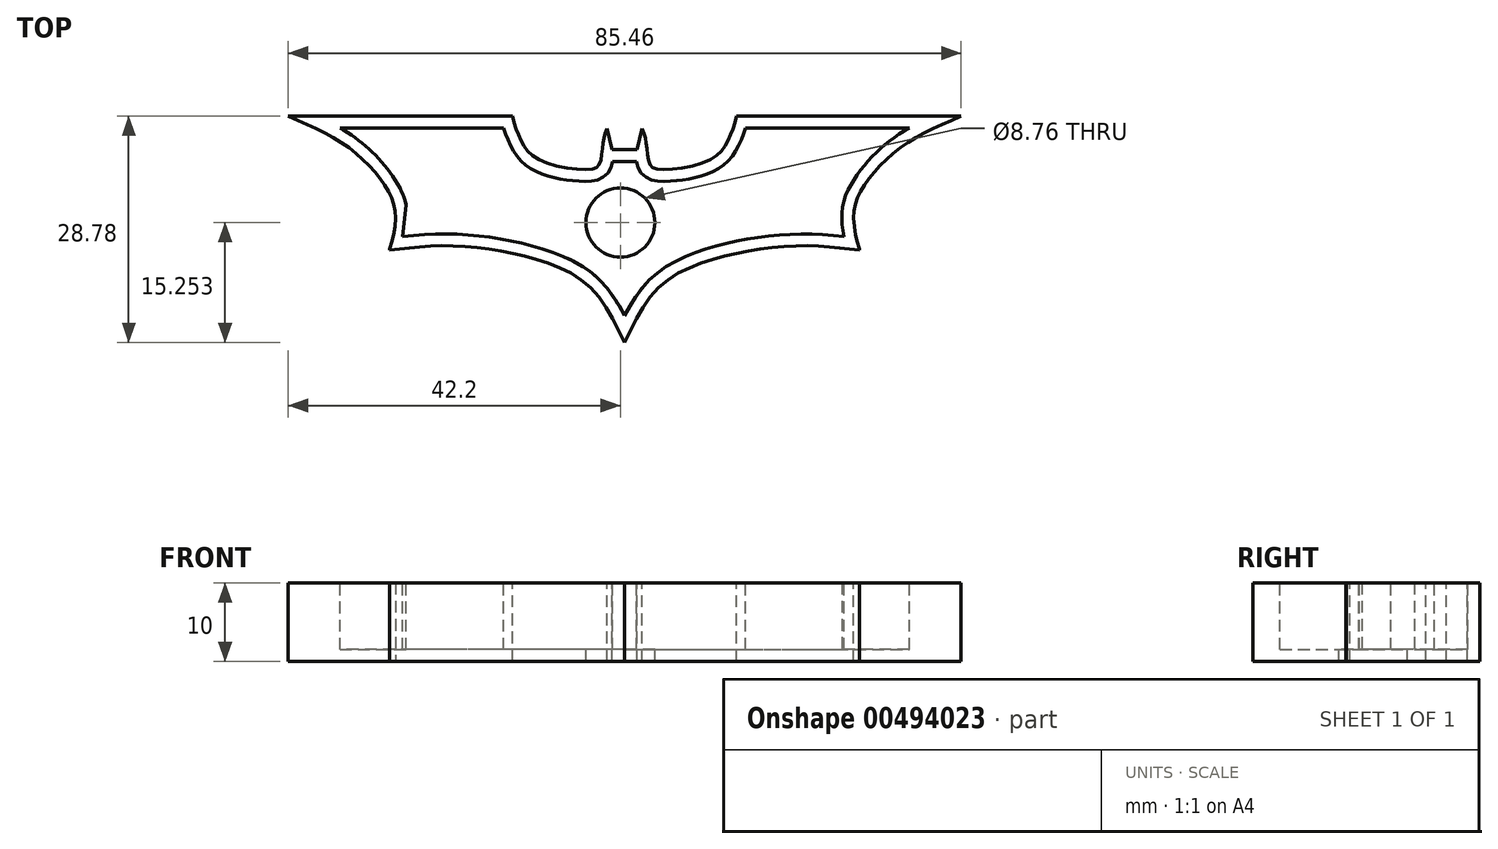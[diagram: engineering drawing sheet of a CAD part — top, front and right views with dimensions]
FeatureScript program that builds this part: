
annotation { "Feature Type Name" : "Feature", "Feature Type Description" : "" }
export const myFeature = defineFeature(function(context is Context, id is Id, definition is map)
    precondition{}
    {
        {
            var Q0;
            Q0=qCreatedBy(makeId("Top.planeOp"),FACE);
            var sketch = newSketch(context, id + "F0", { "sketchPlane" : qUnion([Q0])});
            skLineSegment(sketch, "E0", {"start": v(14.74, 30.46) * mm, "end": v(43.26, 30.46) * mm});
            skLineSegment(sketch, "E1", {"start": v(2.76, 28.88) * mm, "end": v(2.1, 26.2) * mm});
            skLineSegment(sketch, "E2", {"start": v(2.1, 26.2) * mm, "end": v(0.53, 26.2) * mm});
            skFitSpline(sketch, "E3", {"points": [v(2.76, 28.88) * mm, v(3.29, 26.93) * mm, v(3.66, 24.48) * mm, v(4.77, 23.7) * mm, v(11.34, 24.86) * mm, v(13.65, 27.35) * mm, v(14.74, 30.46) * mm], "startDerivative": vector(6.7, -15.32) * mm, "endDerivative": vector(3.76, 19.58) * mm});
            skFitSpline(sketch, "E4", {"points": [v(43.26, 30.46) * mm, v(35.41, 26.33) * mm, v(30.8, 21.36) * mm, v(29.65, 16.93) * mm, v(30.37, 13.56) * mm], "startDerivative": vector(-28.89, -12.67) * mm, "endDerivative": vector(-0.18, 1.77) * mm});
            skLineSegment(sketch, "E5", {"start": v(0.53, 1.68) * mm, "end": v(0.53, 33.7) * mm, "construction": true});
            skFitSpline(sketch, "E6", {"points": [v(0.53, 1.68) * mm, v(4.86, 8.68) * mm, v(11.35, 12.14) * mm, v(18.49, 13.66) * mm, v(25.2, 13.95) * mm, v(30.38, 13.45) * mm], "startDerivative": vector(16.88, 35.7) * mm, "endDerivative": vector(28.92, -2.58) * mm});
            skLineSegment(sketch, "E7.MirrorCS", {"start": v(-1.05, 26.2) * mm, "end": v(0.53, 26.2) * mm});
            skLineSegment(sketch, "E8.MirrorCS", {"start": v(-1.7, 28.88) * mm, "end": v(-1.05, 26.2) * mm});
            skFitSpline(sketch, "E9.MirrorCS", {"points": [v(0.53, 1.68) * mm, v(-3.8, 8.68) * mm, v(-10.3, 12.14) * mm, v(-17.43, 13.66) * mm, v(-24.14, 13.95) * mm, v(-29.32, 13.45) * mm], "startDerivative": vector(-16.88, 35.7) * mm, "endDerivative": vector(-28.92, -2.58) * mm});
            skFitSpline(sketch, "E10.MirrorCS", {"points": [v(-1.7, 28.88) * mm, v(-2.23, 26.93) * mm, v(-2.6, 24.48) * mm, v(-3.72, 23.7) * mm, v(-10.28, 24.86) * mm, v(-12.6, 27.35) * mm, v(-13.68, 30.46) * mm], "startDerivative": vector(-6.7, -15.32) * mm, "endDerivative": vector(-3.76, 19.58) * mm});
            skFitSpline(sketch, "E11.MirrorCS", {"points": [v(-42.2, 30.46) * mm, v(-34.36, 26.33) * mm, v(-29.75, 21.36) * mm, v(-28.6, 16.93) * mm, v(-29.31, 13.56) * mm], "startDerivative": vector(28.89, -12.67) * mm, "endDerivative": vector(0.18, 1.77) * mm});
            skLineSegment(sketch, "E12.MirrorCS", {"start": v(-13.68, 30.46) * mm, "end": v(-42.2, 30.46) * mm});
            skLineSegment(sketch, "E13", {"start": v(30.37, 13.56) * mm, "end": v(30.38, 13.45) * mm});
            skLineSegment(sketch, "E14", {"start": v(-29.31, 13.56) * mm, "end": v(-29.32, 13.45) * mm});
            skSolve(sketch);
        }
        {
            var Q0;
            Q0 = qSketchRegion(id + "F0", true);
            extrude(context, id + "F1", {"entities" : qUnion([Q0]), "oppositeDirection" : true, "depth" : 10 * mm});
        }
        {
            var Q0;
            Q0=makeQuery(id+"F1.opExtrude","CAP_FACE",FACE,{"disambiguationData":[OSD([sQuery(id+"F0.wireOp",EDGE,"E0"),sQuery(id+"F0.wireOp",EDGE,"E1"),sQuery(id+"F0.wireOp",EDGE,"E2"),sQuery(id+"F0.wireOp",EDGE,"E3"),sQuery(id+"F0.wireOp",EDGE,"E4"),sQuery(id+"F0.wireOp",EDGE,"E6"),sQuery(id+"F0.wireOp",EDGE,"E7.MirrorCS"),sQuery(id+"F0.wireOp",EDGE,"E8.MirrorCS"),sQuery(id+"F0.wireOp",EDGE,"E9.MirrorCS"),sQuery(id+"F0.wireOp",EDGE,"E10.MirrorCS"),sQuery(id+"F0.wireOp",EDGE,"E11.MirrorCS"),sQuery(id+"F0.wireOp",EDGE,"E12.MirrorCS"),sQuery(id+"F0.wireOp",EDGE,"E13"),sQuery(id+"F0.wireOp",EDGE,"E14")])],"isStart":true});
            shell(context, id + "F2", {"entities" : qUnion([Q0]), "thickness" : 1.5 * mm});
        }
        {
            var Q0;
            Q0=makeQuery(id+"F2.opShell","OFFSET_FACE",FACE,{"disambiguationData":[OSD([sQuery(id+"F0.wireOp",EDGE,"E0"),sQuery(id+"F0.wireOp",EDGE,"E1"),sQuery(id+"F0.wireOp",EDGE,"E2"),sQuery(id+"F0.wireOp",EDGE,"E3"),sQuery(id+"F0.wireOp",EDGE,"E4"),sQuery(id+"F0.wireOp",EDGE,"E6"),sQuery(id+"F0.wireOp",EDGE,"E7.MirrorCS"),sQuery(id+"F0.wireOp",EDGE,"E8.MirrorCS"),sQuery(id+"F0.wireOp",EDGE,"E9.MirrorCS"),sQuery(id+"F0.wireOp",EDGE,"E10.MirrorCS"),sQuery(id+"F0.wireOp",EDGE,"E11.MirrorCS"),sQuery(id+"F0.wireOp",EDGE,"E12.MirrorCS"),sQuery(id+"F0.wireOp",EDGE,"E13"),sQuery(id+"F0.wireOp",EDGE,"E14")])]});
            var sketch = newSketch(context, id + "F3", { "sketchPlane" : qUnion([Q0])});
            skCircle(sketch, "E15", {"center": v(0, 16.93) * mm, "radius": 4.38 * mm});
            skSolve(sketch);
        }
        {
            var Q0;
            Q0 = qSketchRegion(id + "F3", true);
            extrude(context, id + "F4", {"entities" : qUnion([Q0]), "operationType" : NewBodyOperationType.REMOVE, "oppositeDirection" : true, "depth" : 5 * mm});
        }
    });
